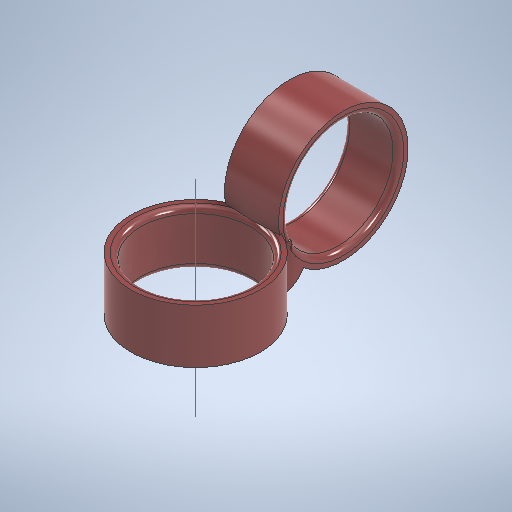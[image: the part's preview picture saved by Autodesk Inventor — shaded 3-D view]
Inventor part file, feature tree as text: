
AUTODESK INVENTOR PART (.ipt)
format: ipt  version: 2025.2 (Build 292293000, 293)  size: 365,568 bytes
history: native  units: in
note: dims shown in document units (in); Inventor stores cm internally (conversion verified against a paired STEP export)
features: sketch x5, extrude x4, plane x3, fillet x3, other x1
ambient origin geometry x8: Origin, YZ Plane, XZ Plane, XY Plane, X Axis, Y Axis, Z Axis, Center Point
bodies: Solid1 (feature_tree)
feature tree (16):
  extrude  "Extrusion1"  Depth=0.6in
  sketch  "Sketch5"  dims[d4=0.25in d5=0.0in d7=0.6in]
  plane  "Work Plane4"
  plane  "Work Plane5"
  extrude  "Extrusion2"  Depth=0.6in
  extrude  "Extrusion3"  Depth=0.3in
  fillet  "Fillet1"  Radius=0.3in
  fillet  "Fillet3"  Radius=0.3in
  fillet  "Fillet4"  [1 undecoded]
  extrude  "Extrusion5"  Depth=0.6in
  sketch  "Sketch2"  dims[d2=0.51in d3=0.6in]
  plane  "Work Plane3"
  other  "Work Axis1"
  sketch  "Sketch8"  dims[d8=0.6in d9=0.3in d10=0.3in d11=0.3in d12=90.0deg]
  sketch  "Sketch10"  dims[d13=0.51in d14=0.6in]
  sketch  "Sketch13"  dims[d15=0.3in d16=0.25in d17=0.0in d18=0.074in d19=0.0in d20=0.037in d21=0.0in d22=0.125in d26=0.025in d27=0.025in d28=0.0in d29=0.08in d30=0.0in d31=0.0in d32=0.0in d33=0.0in d34=0.0in]
note: 1 required parameter value undecoded (feature->parameter linkage not recoverable at this tier; creation-order binding heuristic only, values carry confidence <= 0.55)
